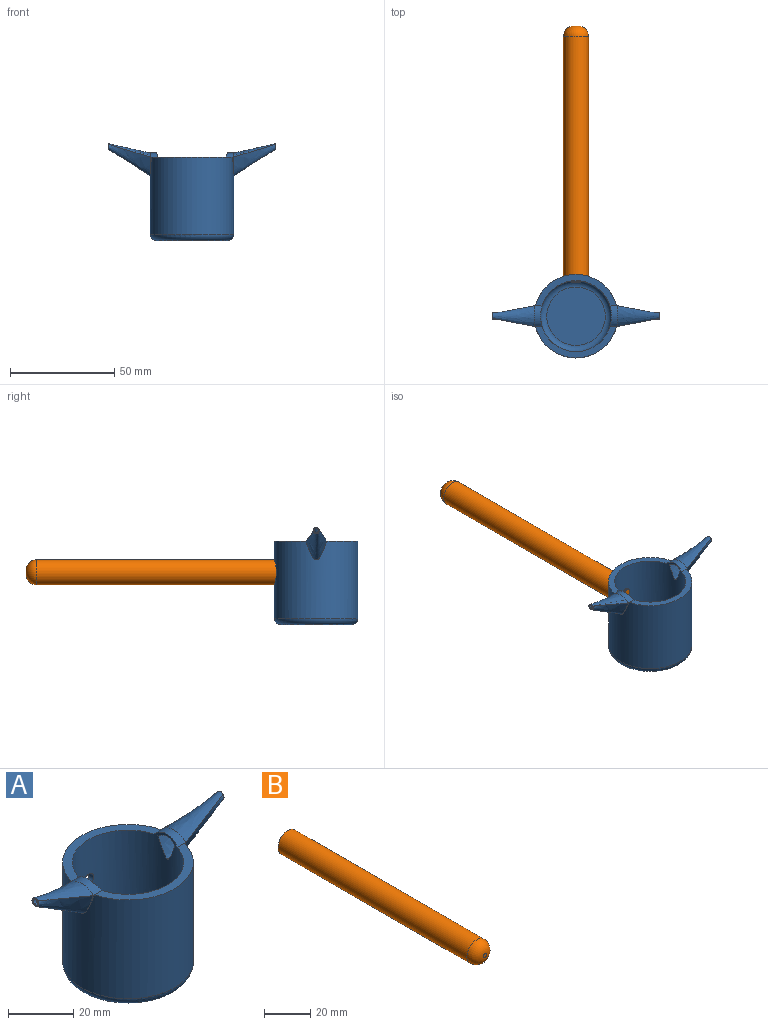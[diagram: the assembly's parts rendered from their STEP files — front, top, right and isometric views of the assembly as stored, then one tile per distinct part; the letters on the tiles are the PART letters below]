
ASSEMBLY  parts=2 mates=1
PART A: 27 faces, bbox 80x43.3x46.5 mm
  f0: cylinder r=17mm len=34mm, axis (0,0,-1), area 3552.4mm2, adj f3,f5,f9,f12,f15,f16,f19,f22
  f1: cylinder r=20mm len=40mm, axis (0,0,-1), area 4444.2mm2, adj f3,f5,f8,f10,f11,f17,f18,f24
  f2: plane 3x3mm, normal (1,0,0), area 3.9mm2, adj f20,f21,f22,f23
  f3: plane 38.73x15mm, normal (0,0,1), area 144mm2, adj f0,f1,f12,f19
  f4: plane 3x3mm, normal (-1,0,0), area 3.9mm2, adj f13,f14,f15,f16
  f5: plane 38.73x15mm, normal (0,0,1), area 144mm2, adj f0,f1,f12,f19
  f6: plane 34x34mm, normal (0,0,-1), area 907.9mm2, adj f8
  f7: plane 28x28mm, normal (0,0,1), area 615.8mm2, adj f9
  f8: torus R=17mm, axis (0,0,1), area 559.9mm2, adj f1,f6
  f9: torus R=14mm, axis (0,0,1), area 471.1mm2, adj f0,f7
  f10: bspline ~9x6.36mm, area 2.9mm2, adj f1,f12,f13
  f11: bspline ~9x5.33mm, area 2.9mm2, adj f1,f12,f13
  f12: bspline ~10x4mm, area 36.1mm2, adj f0,f3,f5,f10,f11,f14
  f13: bspline ~20x15.06mm, area 266.4mm2, adj f4,f10,f11,f14
  f14: bspline ~20x10mm, area 150.9mm2, adj f4,f12,f13
  f15: bspline ~24x13.72mm, area 225.4mm2, adj f0,f4,f16
  f16: bspline ~23.4x7.29mm, area 120.1mm2, adj f0,f4,f15
  f17: bspline ~9x5.33mm, area 2.9mm2, adj f1,f19,f20
  f18: bspline ~9x6.36mm, area 2.9mm2, adj f1,f19,f20
  f19: bspline ~10x4mm, area 36.1mm2, adj f0,f3,f5,f17,f18,f21
  f20: bspline ~20x15.06mm, area 266.4mm2, adj f2,f17,f18,f21
  f21: bspline ~20x10mm, area 150.9mm2, adj f2,f19,f20
  f22: bspline ~24x13.72mm, area 225.4mm2, adj f0,f2,f23
  f23: bspline ~23.4x7.29mm, area 120.1mm2, adj f0,f2,f22
  f24: cylinder r=6mm len=12mm, axis (0,1,0), area 20.4mm2, adj f1,f25
  f25: plane 12x12mm, normal (0,1,0), area 99.2mm2, adj f24,f26
  f26: cylinder r=2.1mm len=4.2mm, axis (0,1,0), area 26.4mm2, adj f0,f25
PART B: 8 faces, bbox 12x123x12 mm
  f0: cylinder r=6mm len=115mm, axis (0,1,0), area 4335.4mm2, adj f2,f3
  f1: plane 2x2mm, normal (0,-1,0), area 3.1mm2, adj f3
  f2: plane 12x12mm, normal (0,1,0), area 84.8mm2, adj f0,f6
  f3: torus R=1mm, axis (0,-1,0), area 206.4mm2, adj f0,f1
  f4: cylinder r=2.5mm len=5mm, axis (0,-1,0), area 31.4mm2, adj f6,f7
  f5: plane 4x4mm, normal (0,1,0), area 12.6mm2, adj f7
  f6: cone r=3mm half-angle=45deg, axis (0,-1,0), area 12.2mm2, adj f2,f4
  f7: cone r=2.5mm half-angle=45deg, axis (0,-1,0), area 10mm2, adj f4,f5
PLACE A at identity fixed
PLACE B rot(axis=(1,0,0),180deg) t=(0,19,25)mm
MATE fastened B.f0 <-> A.f24  axis (0,-1,0) through (0,19,25)mm
